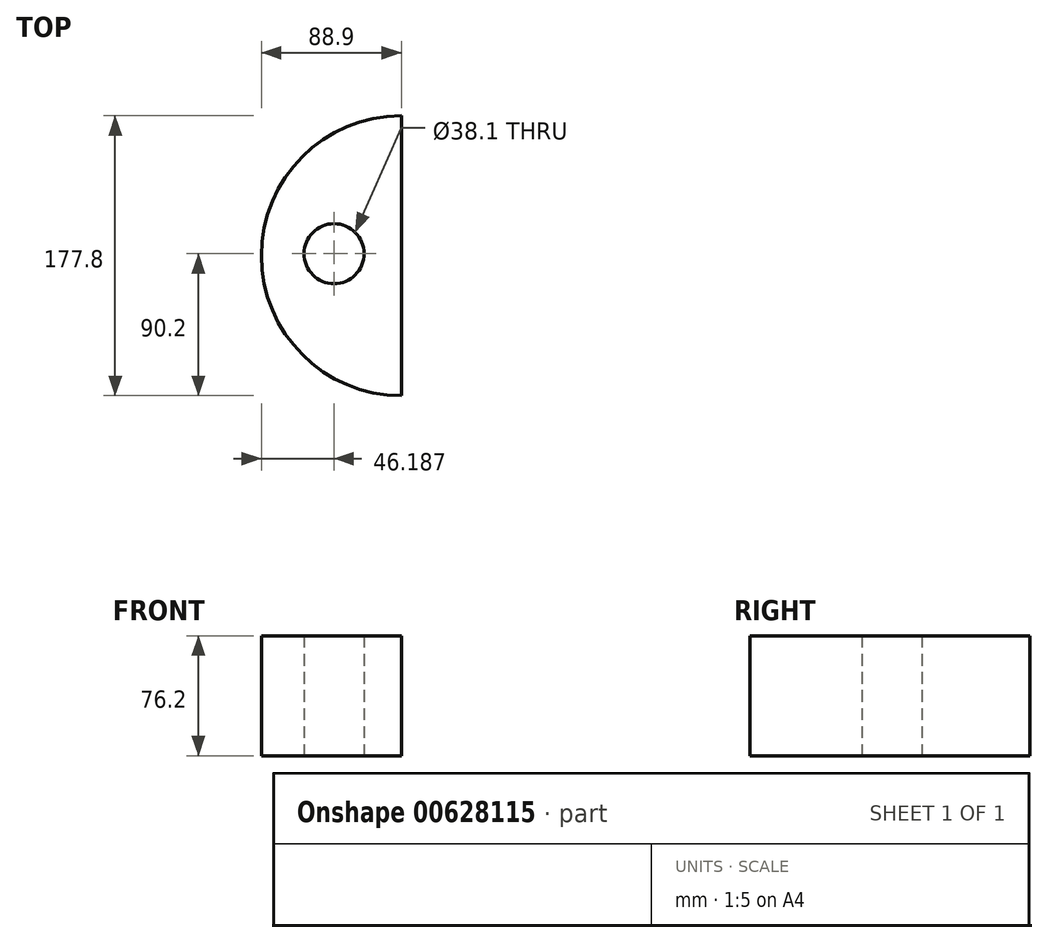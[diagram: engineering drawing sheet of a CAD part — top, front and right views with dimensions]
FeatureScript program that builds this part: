
annotation { "Feature Type Name" : "Feature", "Feature Type Description" : "" }
export const myFeature = defineFeature(function(context is Context, id is Id, definition is map)
    precondition{}
    {
        {
            var Q0;
            Q0=qCreatedBy(makeId("Top.planeOp"),FACE);
            var sketch = newSketch(context, id + "F0", { "sketchPlane" : qUnion([Q0])});
            skArc(sketch, "E0", {"start": v(0, 99.54) * mm, "mid": v(-88.9, 10.64) * mm, "end": v(0, -78.26) * mm});
            skLineSegment(sketch, "E1", {"start": v(0, -78.26) * mm, "end": v(0, 99.54) * mm});
            skCircle(sketch, "E2", {"center": v(-42.71, 11.94) * mm, "radius": 19.05 * mm});
            skSolve(sketch);
        }
        {
            var Q0;
            Q0=makeQuery(id+"F0.imprint","IMPRINT",FACE,{"disambiguationData":[TD([[makeQuery(id+"F0.imprint","IMPRINT",EDGE,{"derivedFrom":sQuery(id+"F0.wireOp",EDGE,"E0")}),1.0]])]});
            extrude(context, id + "F1", {"entities" : qUnion([Q0]), "depth" : 76.2 * mm, "offsetDistance" : 25.4 * mm});
        }
    });
